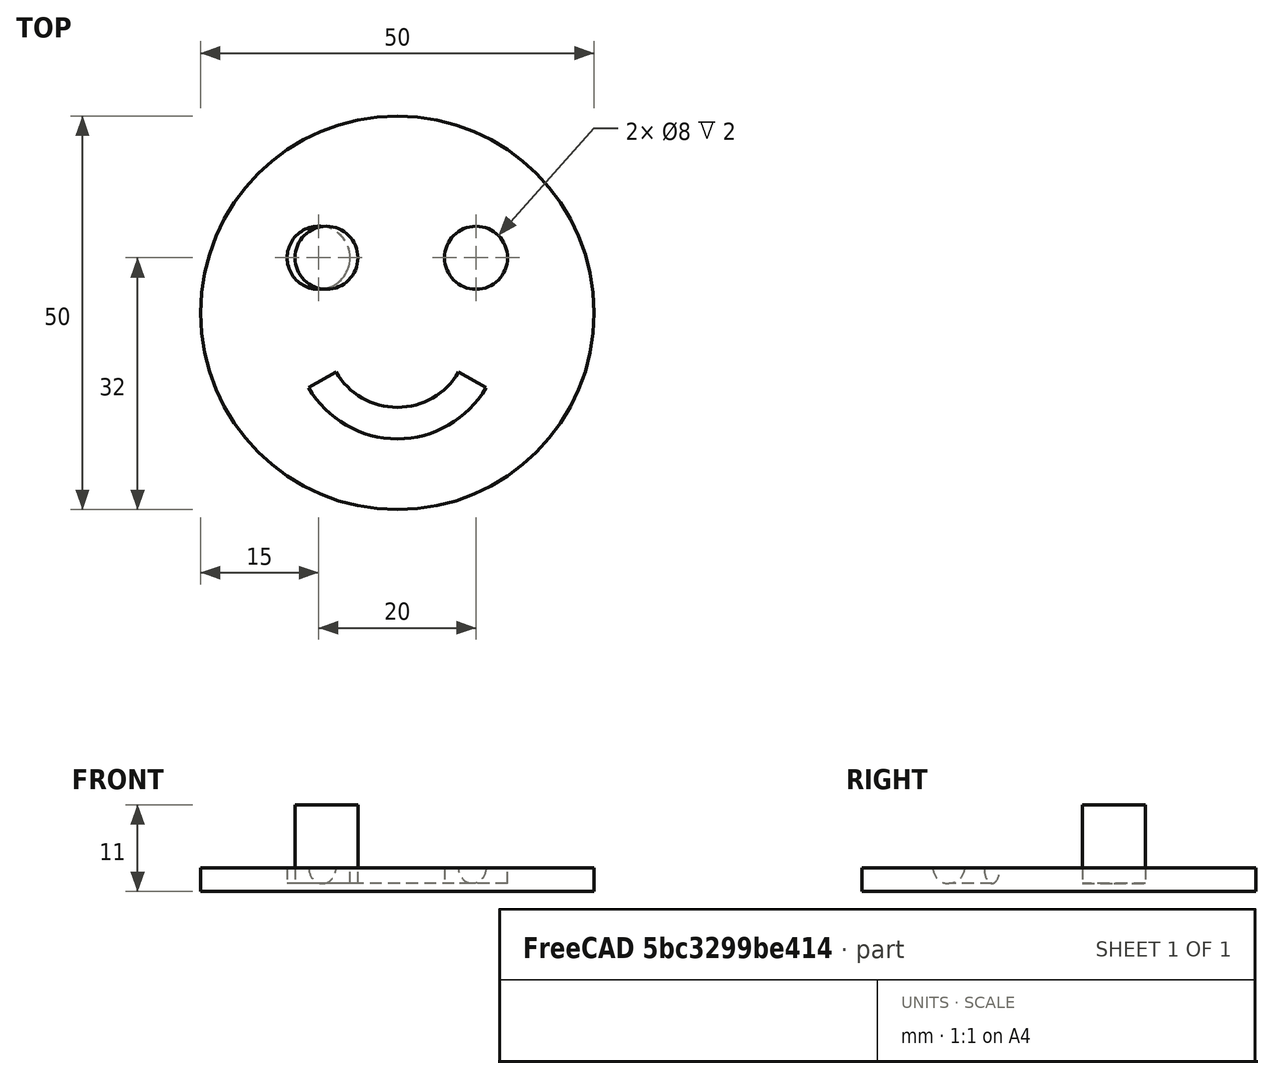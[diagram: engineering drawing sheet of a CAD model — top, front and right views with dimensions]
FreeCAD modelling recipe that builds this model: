
FCSTD DOCUMENT  (FreeCAD 1.0R39319 (Git))
Label: ojt1_r01_smile
License: All rights reserved
LicenseURL: https://en.wikipedia.org/wiki/All_rights_reserved
objects: Part::Cylinder×2, Part::Cut×2, Part::FeaturePython×1, Part::Torus×1
note: 5 computed .brp shape members not serialized (recipe doc carries the construction recipe); baked Part::Feature solids carry a one-line shape summary decoded from their .brp

FEATURE [Part::Cylinder] Cylinder  label="Cilindre"
  Angle = 360
  AttacherType = Attacher::AttachEngine3D
  FirstAngle = 0
  Height = 3
  Radius = 25
  SecondAngle = 0
FEATURE [Part::Cylinder] Cylinder001  label="Cilindre001"
  Angle = 360
  AttacherType = Attacher::AttachEngine3D
  FirstAngle = 0
  Height = 10
  Placement = pos=(-9,7,1) rot=(0,0,1;0rad)
  Radius = 4
  SecondAngle = 0
FEATURE [Part::FeaturePython] Array  label="ulls"  # Draft array (typed FeaturePython)
  AlwaysSyncPlacement = false
  Angle = 360
  ArrayType = 0
  Axis = (0,0,1)
  Base = -> Cylinder001
  Center = (0,0,0)
  Count = 2
  ExpandArray = false
  Fuse = false
  IntervalAxis = (0,0,0)
  IntervalX = (20,0,0)
  IntervalY = (0,0,0)
  IntervalZ = (0,0,100)
  NumberCircles = 3
  NumberPolar = 5
  NumberX = 2
  NumberY = 1
  NumberZ = 1
  Placement = pos=(-1,0,0) rot=(0,0,1;0rad)
  PlacementList = 2 placements: [(-9,7,1),(11,7,1)]
  RadialDistance = 50
  ScaleList = (2) [(1,1,1),(1,1,1)]
  Symmetry = 1
  TangentialDistance = 25
FEATURE [Part::Torus] Torus
  Angle1 = -180
  Angle2 = 180
  Angle3 = 120
  AttacherType = Attacher::AttachEngine3D
  Placement = pos=(0,-3,3) rot=(0,0,-1;2.61799rad)
  Radius1 = 11
  Radius2 = 2
FEATURE [Part::Cut] Cut
  Base = -> Cylinder
  Tool = -> Array
FEATURE [Part::Cut] Cut001  label="cara final"
  Base = -> Cut
  Tool = -> Torus
